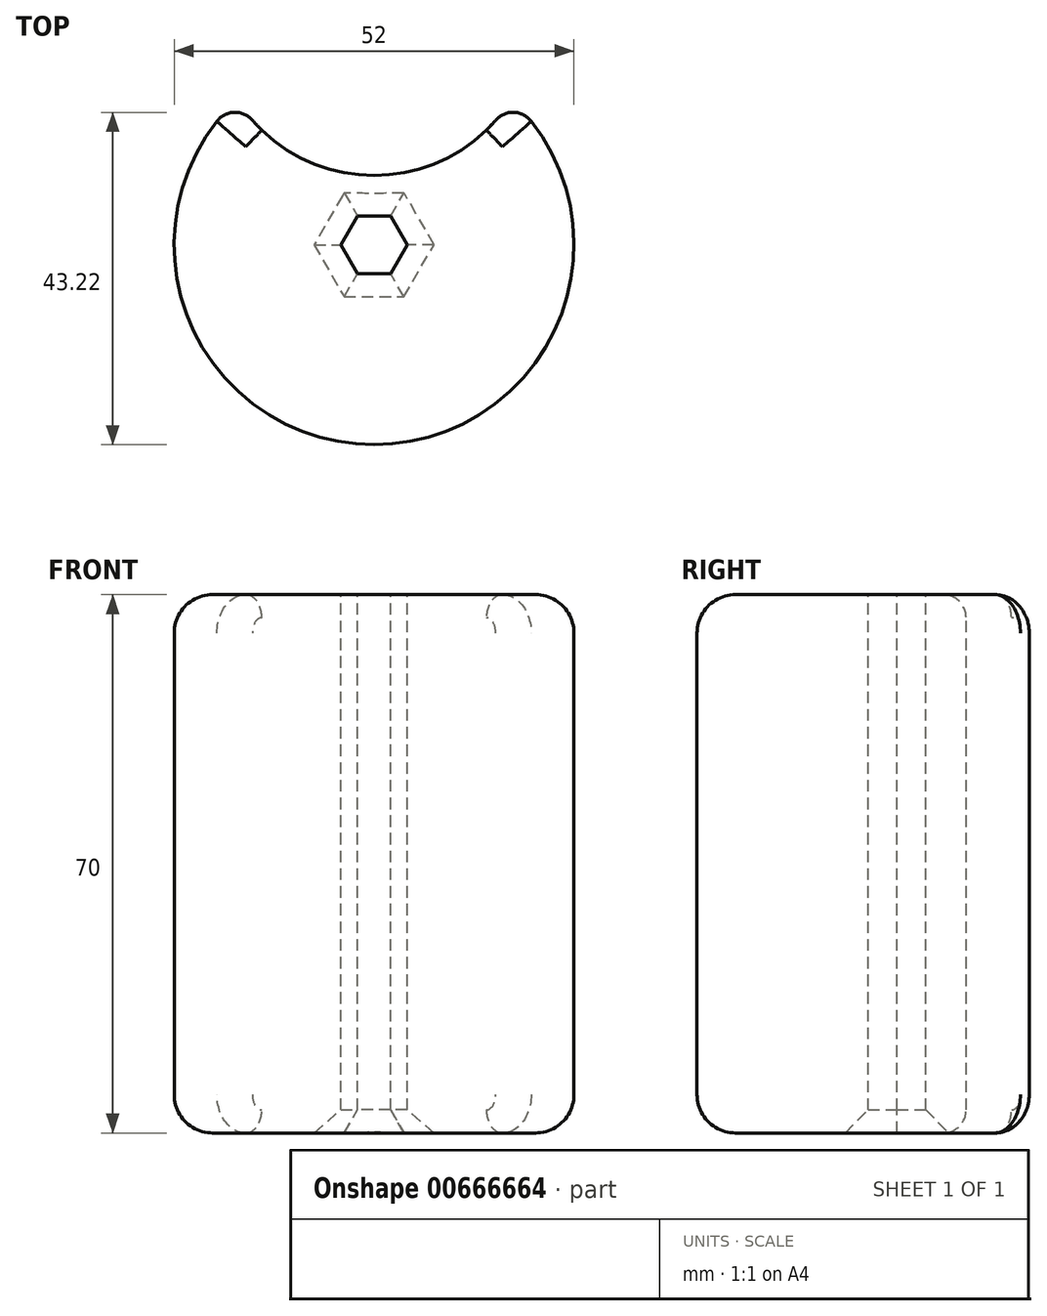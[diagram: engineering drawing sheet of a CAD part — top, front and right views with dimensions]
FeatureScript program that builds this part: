
annotation { "Feature Type Name" : "Feature", "Feature Type Description" : "" }
export const myFeature = defineFeature(function(context is Context, id is Id, definition is map)
    precondition{}
    {
        {
            var Q0;
            Q0=qCreatedBy(makeId("Top.planeOp"),FACE);
            var sketch = newSketch(context, id + "F0", { "sketchPlane" : qUnion([Q0])});
            skCircle(sketch, "E0", {"center": v(0, 0) * mm, "radius": 26 * mm});
            skSolve(sketch);
        }
        {
            var Q0;
            Q0 = qSketchRegion(id + "F0", true);
            extrude(context, id + "F1", {"entities" : qUnion([Q0]), "endBound" : BoundingType.SYMMETRIC, "depth" : 70 * mm, "offsetDistance" : 25 * mm});
        }
        {
            var Q0;
            Q0=makeQuery(id+"F1.opExtrude","CAP_FACE",FACE,{"disambiguationData":[OSD([sQuery(id+"F0.wireOp",EDGE,"E0")])],"isStart":false});
            var sketch = newSketch(context, id + "F2", { "sketchPlane" : qUnion([Q0])});
            skCircle(sketch, "E1.cCircle", {"center": v(0, 0) * mm, "radius": 3.75 * mm, "construction": true});
            skLineSegment(sketch, "E1.0", {"start": v(-4.33, 0) * mm, "end": v(-2.17, 3.75) * mm});
            skLineSegment(sketch, "E1.1", {"start": v(-2.17, 3.75) * mm, "end": v(2.17, 3.75) * mm});
            skLineSegment(sketch, "E1.2", {"start": v(2.17, 3.75) * mm, "end": v(4.33, 0) * mm});
            skLineSegment(sketch, "E1.3", {"start": v(4.33, 0) * mm, "end": v(2.17, -3.75) * mm});
            skLineSegment(sketch, "E1.4", {"start": v(2.17, -3.75) * mm, "end": v(-2.17, -3.75) * mm});
            skLineSegment(sketch, "E1.5", {"start": v(-2.17, -3.75) * mm, "end": v(-4.33, 0) * mm});
            skPoint(sketch, "E1.0.midPoint", {"position": v(-3.25, 1.88) * mm});
            skSolve(sketch);
        }
        {
            var Q0;
            Q0 = qSketchRegion(id + "F2", true);
            extrude(context, id + "F3", {"entities" : qUnion([Q0]), "operationType" : NewBodyOperationType.REMOVE, "endBound" : BoundingType.THROUGH_ALL, "oppositeDirection" : true, "depth" : 25 * mm, "offsetDistance" : 25 * mm});
        }
        {
            var Q0;
            Q0=makeQuery(id+"F1.opExtrude","CAP_FACE",FACE,{"disambiguationData":[OSD([sQuery(id+"F0.wireOp",EDGE,"E0")])],"isStart":false});
            cPlane(context, id + "F4", {"entities" : qUnion([Q0]), "cplaneType" : CPlaneType.OFFSET, "offset" : 5 * mm, "width" : 150 * mm, "height" : 150 * mm});
        }
        {
            var Q0;
            Q0=qCreatedBy(id+"F4.planeOp",FACE);
            var sketch = newSketch(context, id + "F5", { "sketchPlane" : qUnion([Q0])});
            skCircle(sketch, "E2", {"center": v(0, 30) * mm, "radius": 21 * mm});
            skPoint(sketch, "E3.center", {"position": v(0, 0) * mm});
            skSolve(sketch);
        }
        {
            var Q0;
            Q0 = qSketchRegion(id + "F5", true);
            extrude(context, id + "F6", {"entities" : qUnion([Q0]), "operationType" : NewBodyOperationType.REMOVE, "endBound" : BoundingType.THROUGH_ALL, "oppositeDirection" : true, "depth" : 25 * mm, "offsetDistance" : 25 * mm});
        }
        {
            var Q0;
            Q0=makeQuery(id+"F6.boolean.opBoolean","COPY",FACE,{"derivedFrom":makeQuery(id+"F6.opExtrude","SWEPT_FACE",FACE,{"disambiguationData":[OSD([sQuery(id+"F5.wireOp",EDGE,"E2")])]})});
            fillet(context, id + "F7", {"entities" : qUnion([Q0]), "radius" : 3 * mm, "tangentPropagation" : true, "allowEdgeOverflow" : false});
        }
        {
            var Q0;
            Q0=qCreatedBy(makeId("Right.planeOp"),FACE);
            var sketch = newSketch(context, id + "F8", { "sketchPlane" : qUnion([Q0])});
            skLineSegment(sketch, "E4", {"start": v(0, 56.02) * mm, "end": v(0, -63.98) * mm, "construction": true});
            skSolve(sketch);
        }
        {
            var Q0;
            {var subQ0=sQuery(id+"F0.wireOp",EDGE,"E0");var subQ1=makeQuery(id+"F1.opExtrude","SWEPT_FACE",FACE,{"disambiguationData":[OSD([subQ0])]});var subQ2=sQuery(id+"F5.wireOp",EDGE,"E2");Q0=makeQuery(id+"Fl9d2EtmhdIW2hl_1.1.F6.boolean.opBoolean","SPLIT",EDGE,{"disambiguationData":[TD([makeQuery(id+"F7.opFillet","BLEND_FACE",FACE,{"disambiguationData":[OSD([subQ0,subQ2]),TDD([makeQuery(id+"F6.boolean.opBoolean","INTERSECT",EDGE,{"disambiguationData":[OD(1.0)],"derivedFrom":[subQ1,makeQuery(id+"F6.opExtrude","SWEPT_FACE",FACE,{"disambiguationData":[OSD([subQ2])]})]})])]})])],"derivedFrom":makeQuery(id+"F1.opExtrude","CAP_EDGE",EDGE,{"disambiguationData":[OSD([subQ0])],"isStart":false})});}
            var Q1;
            {var subQ0=sQuery(id+"F0.wireOp",EDGE,"E0");var subQ1=makeQuery(id+"F1.opExtrude","SWEPT_FACE",FACE,{"disambiguationData":[OSD([subQ0])]});var subQ2=sQuery(id+"F5.wireOp",EDGE,"E2");var subQ4=makeQuery(id+"Fl9d2EtmhdIW2hl_1.1.F6.opExtrude","SWEPT_FACE",FACE,{"disambiguationData":[OSD([subQ2])]});Q1=makeQuery(id+"Fl9d2EtmhdIW2hl_1.2.F6.boolean.opBoolean","SPLIT",EDGE,{"disambiguationData":[TD([makeQuery(id+"Fl9d2EtmhdIW2hl_1.1.F7.opFillet","BLEND_FACE",FACE,{"disambiguationData":[OSD([subQ0,subQ2]),TDD([makeQuery(id+"Fl9d2EtmhdIW2hl_1.1.F6.boolean.opBoolean","INTERSECT",EDGE,{"disambiguationData":[OD(0.0)],"derivedFrom":[subQ1,subQ4]})])]})])],"derivedFrom":makeQuery(id+"Fl9d2EtmhdIW2hl_1.1.F6.boolean.opBoolean","SPLIT",EDGE,{"disambiguationData":[TD([makeQuery(id+"F7.opFillet","BLEND_FACE",FACE,{"disambiguationData":[OSD([subQ0,subQ2]),TDD([makeQuery(id+"F6.boolean.opBoolean","INTERSECT",EDGE,{"disambiguationData":[OD(0.0)],"derivedFrom":[subQ1,makeQuery(id+"F6.opExtrude","SWEPT_FACE",FACE,{"disambiguationData":[OSD([subQ2])]})]})])]})])],"derivedFrom":makeQuery(id+"F1.opExtrude","CAP_EDGE",EDGE,{"disambiguationData":[OSD([subQ0])],"isStart":false})})});}
            var Q2;
            {var subQ0=sQuery(id+"F0.wireOp",EDGE,"E0");var subQ1=makeQuery(id+"F1.opExtrude","SWEPT_FACE",FACE,{"disambiguationData":[OSD([subQ0])]});var subQ2=sQuery(id+"F5.wireOp",EDGE,"E2");var subQ4=makeQuery(id+"F7.opFillet","BLEND_FACE",FACE,{"disambiguationData":[OSD([subQ0,subQ2]),TDD([makeQuery(id+"F6.boolean.opBoolean","INTERSECT",EDGE,{"disambiguationData":[OD(0.0)],"derivedFrom":[subQ1,makeQuery(id+"F6.opExtrude","SWEPT_FACE",FACE,{"disambiguationData":[OSD([subQ2])]})]})])]});Q2=makeQuery(id+"Fl9d2EtmhdIW2hl_1.2.F6.boolean.opBoolean","SPLIT",EDGE,{"disambiguationData":[TD([subQ4])],"derivedFrom":makeQuery(id+"Fl9d2EtmhdIW2hl_1.1.F6.boolean.opBoolean","SPLIT",EDGE,{"disambiguationData":[TD([subQ4])],"derivedFrom":makeQuery(id+"F1.opExtrude","CAP_EDGE",EDGE,{"disambiguationData":[OSD([subQ0])],"isStart":false})})});}
            var Q3;
            {var subQ0=sQuery(id+"F0.wireOp",EDGE,"E0");var subQ1=makeQuery(id+"F1.opExtrude","SWEPT_FACE",FACE,{"disambiguationData":[OSD([subQ0])]});var subQ2=sQuery(id+"F5.wireOp",EDGE,"E2");Q3=makeQuery(id+"Fl9d2EtmhdIW2hl_1.1.F6.boolean.opBoolean","SPLIT",EDGE,{"disambiguationData":[TD([makeQuery(id+"F7.opFillet","BLEND_FACE",FACE,{"disambiguationData":[OSD([subQ0,subQ2]),TDD([makeQuery(id+"F6.boolean.opBoolean","INTERSECT",EDGE,{"disambiguationData":[OD(1.0)],"derivedFrom":[subQ1,makeQuery(id+"F6.opExtrude","SWEPT_FACE",FACE,{"disambiguationData":[OSD([subQ2])]})]})])]})])],"derivedFrom":makeQuery(id+"F1.opExtrude","CAP_EDGE",EDGE,{"disambiguationData":[OSD([subQ0])],"isStart":true})});}
            var Q4;
            {var subQ0=sQuery(id+"F0.wireOp",EDGE,"E0");var subQ1=makeQuery(id+"F1.opExtrude","SWEPT_FACE",FACE,{"disambiguationData":[OSD([subQ0])]});var subQ2=sQuery(id+"F5.wireOp",EDGE,"E2");var subQ4=makeQuery(id+"F7.opFillet","BLEND_FACE",FACE,{"disambiguationData":[OSD([subQ0,subQ2]),TDD([makeQuery(id+"F6.boolean.opBoolean","INTERSECT",EDGE,{"disambiguationData":[OD(0.0)],"derivedFrom":[subQ1,makeQuery(id+"F6.opExtrude","SWEPT_FACE",FACE,{"disambiguationData":[OSD([subQ2])]})]})])]});Q4=makeQuery(id+"Fl9d2EtmhdIW2hl_1.2.F6.boolean.opBoolean","SPLIT",EDGE,{"disambiguationData":[TD([subQ4])],"derivedFrom":makeQuery(id+"Fl9d2EtmhdIW2hl_1.1.F6.boolean.opBoolean","SPLIT",EDGE,{"disambiguationData":[TD([subQ4])],"derivedFrom":makeQuery(id+"F1.opExtrude","CAP_EDGE",EDGE,{"disambiguationData":[OSD([subQ0])],"isStart":true})})});}
            var Q5;
            {var subQ0=sQuery(id+"F0.wireOp",EDGE,"E0");var subQ1=makeQuery(id+"F1.opExtrude","SWEPT_FACE",FACE,{"disambiguationData":[OSD([subQ0])]});var subQ2=sQuery(id+"F5.wireOp",EDGE,"E2");var subQ4=makeQuery(id+"Fl9d2EtmhdIW2hl_1.1.F6.opExtrude","SWEPT_FACE",FACE,{"disambiguationData":[OSD([subQ2])]});Q5=makeQuery(id+"Fl9d2EtmhdIW2hl_1.2.F6.boolean.opBoolean","SPLIT",EDGE,{"disambiguationData":[TD([makeQuery(id+"Fl9d2EtmhdIW2hl_1.1.F7.opFillet","BLEND_FACE",FACE,{"disambiguationData":[OSD([subQ0,subQ2]),TDD([makeQuery(id+"Fl9d2EtmhdIW2hl_1.1.F6.boolean.opBoolean","INTERSECT",EDGE,{"disambiguationData":[OD(0.0)],"derivedFrom":[subQ1,subQ4]})])]})])],"derivedFrom":makeQuery(id+"Fl9d2EtmhdIW2hl_1.1.F6.boolean.opBoolean","SPLIT",EDGE,{"disambiguationData":[TD([makeQuery(id+"F7.opFillet","BLEND_FACE",FACE,{"disambiguationData":[OSD([subQ0,subQ2]),TDD([makeQuery(id+"F6.boolean.opBoolean","INTERSECT",EDGE,{"disambiguationData":[OD(0.0)],"derivedFrom":[subQ1,makeQuery(id+"F6.opExtrude","SWEPT_FACE",FACE,{"disambiguationData":[OSD([subQ2])]})]})])]})])],"derivedFrom":makeQuery(id+"F1.opExtrude","CAP_EDGE",EDGE,{"disambiguationData":[OSD([subQ0])],"isStart":true})})});}
            fillet(context, id + "F9", {"entities" : qUnion([Q0, Q1, Q2, Q3, Q4, Q5]), "radius" : 5 * mm, "tangentPropagation" : true, "allowEdgeOverflow" : false});
        }
        {
            var Q0;
            Q0=makeQuery(id+"F3.boolean.opBoolean","COPY",EDGE,{"derivedFrom":makeQuery(id+"F3.opExtrude","CAP_EDGE",EDGE,{"disambiguationData":[OSD([sQuery(id+"F2.wireOp",EDGE,"E1.2")])],"isStart":true})});
            var Q1;
            Q1=makeQuery(id+"F3.boolean.opBoolean","COPY",EDGE,{"derivedFrom":makeQuery(id+"F3.opExtrude","CAP_EDGE",EDGE,{"disambiguationData":[OSD([sQuery(id+"F2.wireOp",EDGE,"E1.1")])],"isStart":true})});
            var Q2;
            Q2=makeQuery(id+"F3.boolean.opBoolean","COPY",EDGE,{"derivedFrom":makeQuery(id+"F3.opExtrude","CAP_EDGE",EDGE,{"disambiguationData":[OSD([sQuery(id+"F2.wireOp",EDGE,"E1.0")])],"isStart":true})});
            var Q3;
            Q3=makeQuery(id+"F3.boolean.opBoolean","COPY",EDGE,{"derivedFrom":makeQuery(id+"F3.opExtrude","CAP_EDGE",EDGE,{"disambiguationData":[OSD([sQuery(id+"F2.wireOp",EDGE,"E1.5")])],"isStart":true})});
            var Q4;
            Q4=makeQuery(id+"F3.boolean.opBoolean","COPY",EDGE,{"derivedFrom":makeQuery(id+"F3.opExtrude","CAP_EDGE",EDGE,{"disambiguationData":[OSD([sQuery(id+"F2.wireOp",EDGE,"E1.4")])],"isStart":true})});
            var Q5;
            Q5=makeQuery(id+"F3.boolean.opBoolean","COPY",EDGE,{"derivedFrom":makeQuery(id+"F3.opExtrude","CAP_EDGE",EDGE,{"disambiguationData":[OSD([sQuery(id+"F2.wireOp",EDGE,"E1.3")])],"isStart":true})});
            var Q6;
            Q6=makeQuery(id+"F3.boolean.opBoolean","INTERSECT",EDGE,{"derivedFrom":[makeQuery(id+"F1.opExtrude","CAP_FACE",FACE,{"disambiguationData":[OSD([sQuery(id+"F0.wireOp",EDGE,"E0")])],"isStart":true}),makeQuery(id+"F3.opExtrude","SWEPT_FACE",FACE,{"disambiguationData":[OSD([sQuery(id+"F2.wireOp",EDGE,"E1.3")])]})]});
            var Q7;
            Q7=makeQuery(id+"F3.boolean.opBoolean","INTERSECT",EDGE,{"derivedFrom":[makeQuery(id+"F1.opExtrude","CAP_FACE",FACE,{"disambiguationData":[OSD([sQuery(id+"F0.wireOp",EDGE,"E0")])],"isStart":true}),makeQuery(id+"F3.opExtrude","SWEPT_FACE",FACE,{"disambiguationData":[OSD([sQuery(id+"F2.wireOp",EDGE,"E1.4")])]})]});
            var Q8;
            Q8=makeQuery(id+"F3.boolean.opBoolean","INTERSECT",EDGE,{"derivedFrom":[makeQuery(id+"F1.opExtrude","CAP_FACE",FACE,{"disambiguationData":[OSD([sQuery(id+"F0.wireOp",EDGE,"E0")])],"isStart":true}),makeQuery(id+"F3.opExtrude","SWEPT_FACE",FACE,{"disambiguationData":[OSD([sQuery(id+"F2.wireOp",EDGE,"E1.5")])]})]});
            var Q9;
            Q9=makeQuery(id+"F3.boolean.opBoolean","INTERSECT",EDGE,{"derivedFrom":[makeQuery(id+"F1.opExtrude","CAP_FACE",FACE,{"disambiguationData":[OSD([sQuery(id+"F0.wireOp",EDGE,"E0")])],"isStart":true}),makeQuery(id+"F3.opExtrude","SWEPT_FACE",FACE,{"disambiguationData":[OSD([sQuery(id+"F2.wireOp",EDGE,"E1.0")])]})]});
            var Q10;
            Q10=makeQuery(id+"F3.boolean.opBoolean","INTERSECT",EDGE,{"derivedFrom":[makeQuery(id+"F1.opExtrude","CAP_FACE",FACE,{"disambiguationData":[OSD([sQuery(id+"F0.wireOp",EDGE,"E0")])],"isStart":true}),makeQuery(id+"F3.opExtrude","SWEPT_FACE",FACE,{"disambiguationData":[OSD([sQuery(id+"F2.wireOp",EDGE,"E1.1")])]})]});
            var Q11;
            Q11=makeQuery(id+"F3.boolean.opBoolean","INTERSECT",EDGE,{"derivedFrom":[makeQuery(id+"F1.opExtrude","CAP_FACE",FACE,{"disambiguationData":[OSD([sQuery(id+"F0.wireOp",EDGE,"E0")])],"isStart":true}),makeQuery(id+"F3.opExtrude","SWEPT_FACE",FACE,{"disambiguationData":[OSD([sQuery(id+"F2.wireOp",EDGE,"E1.2")])]})]});
            chamfer(context, id + "F10", {"entities" : qUnion([Q0, Q1, Q2, Q3, Q4, Q5, Q6, Q7, Q8, Q9, Q10, Q11]), "width" : 3 * mm, "tangentPropagation" : true});
        }
    });
